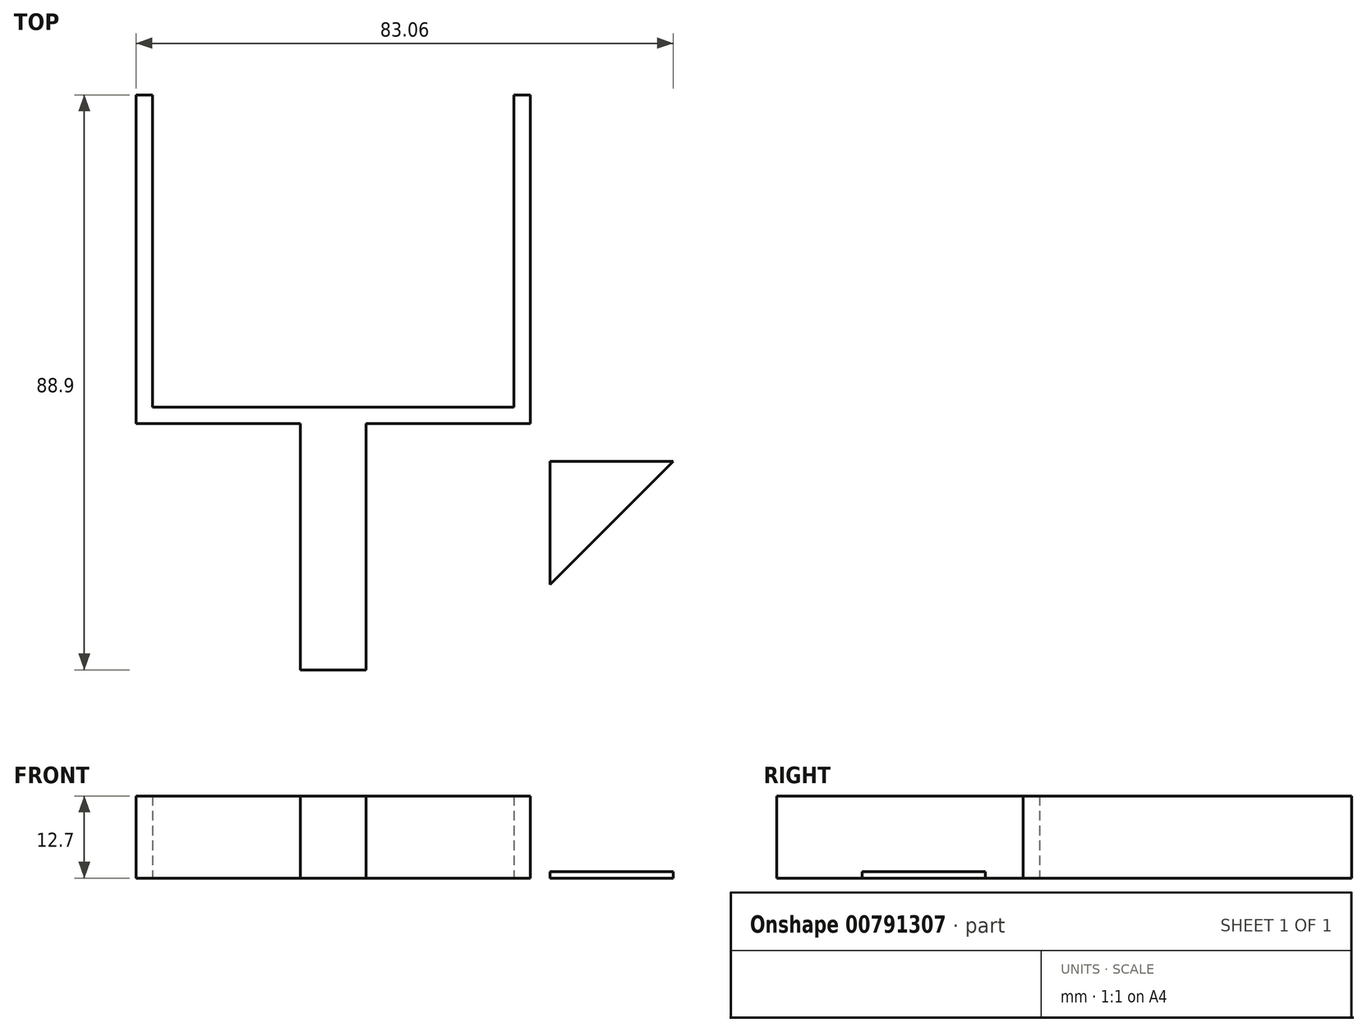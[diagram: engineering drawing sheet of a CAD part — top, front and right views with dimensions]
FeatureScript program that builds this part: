
annotation { "Feature Type Name" : "Feature", "Feature Type Description" : "" }
export const myFeature = defineFeature(function(context is Context, id is Id, definition is map)
    precondition{}
    {
        {
            var Q0;
            Q0=qCreatedBy(makeId("Top.planeOp"),FACE);
            var sketch = newSketch(context, id + "F0", { "sketchPlane" : qUnion([Q0])});
            skLineSegment(sketch, "E0.top", {"start": v(-4.9, -57.2) * mm, "end": v(5.25, -57.2) * mm});
            skLineSegment(sketch, "E0.left", {"start": v(-4.9, -19.1) * mm, "end": v(-4.9, -57.2) * mm});
            skLineSegment(sketch, "E0.right", {"start": v(5.25, -19.1) * mm, "end": v(5.25, -57.2) * mm});
            skLineSegment(sketch, "E1", {"start": v(-30.3, -19.1) * mm, "end": v(-4.9, -19.1) * mm});
            skLineSegment(sketch, "E2", {"start": v(5.25, -19.1) * mm, "end": v(30.65, -19.1) * mm});
            skLineSegment(sketch, "E3", {"start": v(30.65, -19.1) * mm, "end": v(30.65, 31.7) * mm});
            skLineSegment(sketch, "E4", {"start": v(30.65, 31.7) * mm, "end": v(28.11, 31.7) * mm});
            skLineSegment(sketch, "E5", {"start": v(28.11, 31.7) * mm, "end": v(28.11, -16.55) * mm});
            skLineSegment(sketch, "E6", {"start": v(-30.3, -19.1) * mm, "end": v(-30.3, 31.7) * mm});
            skLineSegment(sketch, "E7", {"start": v(-30.3, 31.7) * mm, "end": v(-27.77, 31.7) * mm});
            skLineSegment(sketch, "E8", {"start": v(-27.77, 31.7) * mm, "end": v(-27.77, -16.55) * mm});
            skLineSegment(sketch, "E9", {"start": v(-27.77, -16.55) * mm, "end": v(28.11, -16.55) * mm});
            skPoint(sketch, "E10.start.orphan", {"position": v(30.65, -29.4) * mm});
            skSolve(sketch);
        }
        {
            var Q0;
            Q0 = qSketchRegion(id + "F0", true);
            extrude(context, id + "F1", {"entities" : qUnion([Q0]), "depth" : 12.7 * mm, "offsetDistance" : 25.4 * mm});
        }
        {
            var Q0;
            Q0=qCreatedBy(makeId("Top.planeOp"),FACE);
            var sketch = newSketch(context, id + "F2", { "sketchPlane" : qUnion([Q0])});
            skLineSegment(sketch, "E11", {"start": v(33.7, -24.97) * mm, "end": v(33.7, -44.02) * mm});
            skLineSegment(sketch, "E12", {"start": v(33.7, -24.97) * mm, "end": v(52.75, -24.97) * mm});
            skLineSegment(sketch, "E13", {"start": v(52.75, -24.97) * mm, "end": v(33.7, -44.02) * mm});
            skSolve(sketch);
        }
        {
            var Q0;
            Q0 = qSketchRegion(id + "F2", true);
            extrude(context, id + "F3", {"entities" : qUnion([Q0]), "depth" : 1 * mm, "offsetDistance" : 25.4 * mm});
        }
    });
